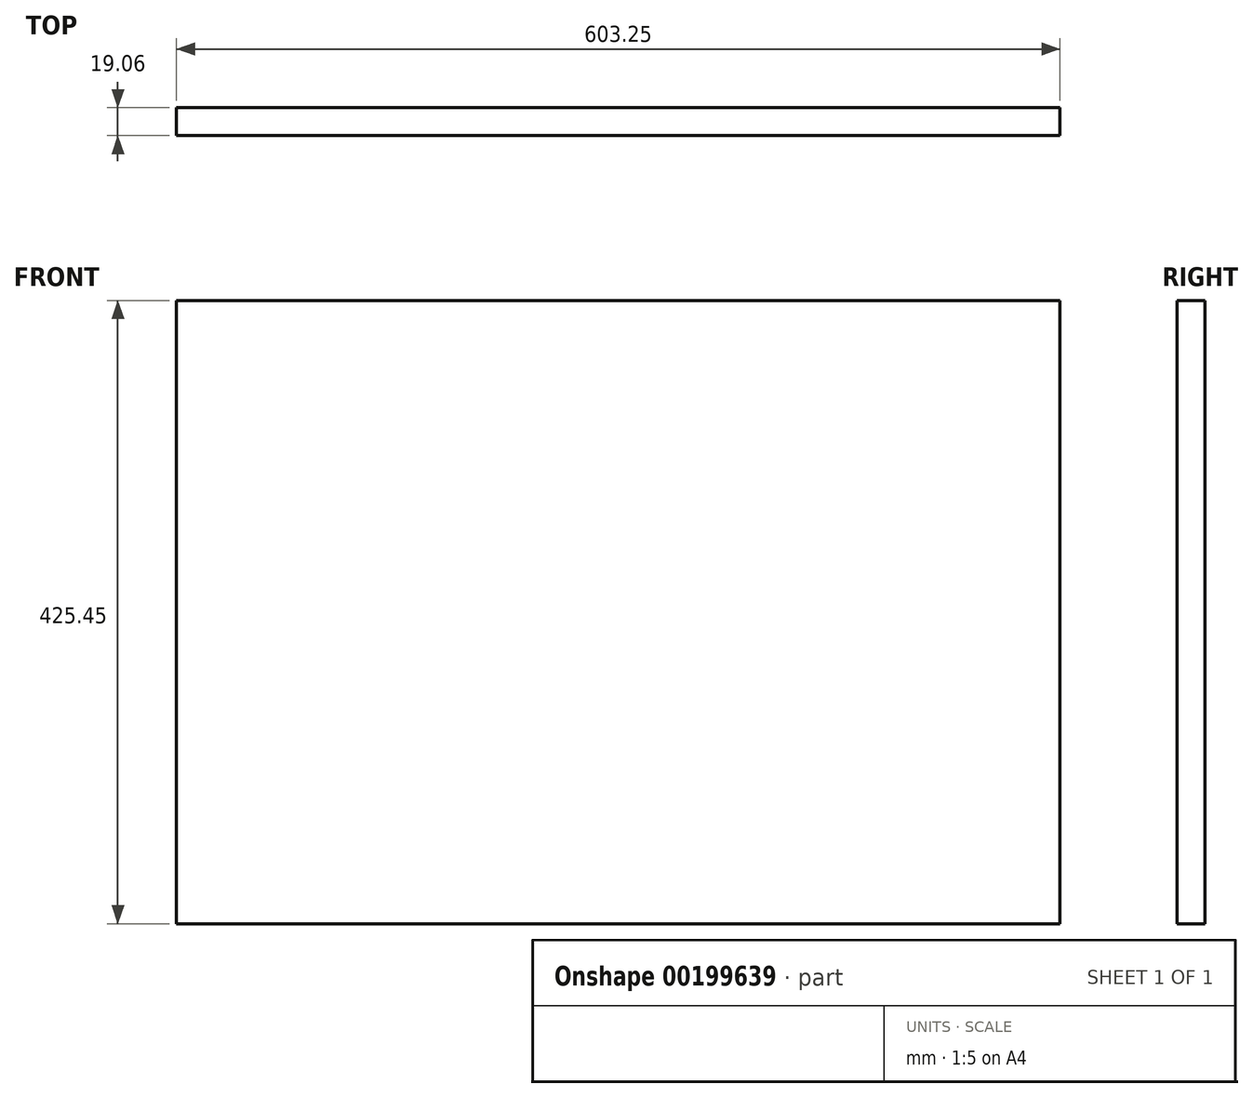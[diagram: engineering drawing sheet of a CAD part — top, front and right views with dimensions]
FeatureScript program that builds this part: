
annotation { "Feature Type Name" : "Feature", "Feature Type Description" : "" }
export const myFeature = defineFeature(function(context is Context, id is Id, definition is map)
    precondition{}
    {
        {
            var Q0;
            Q0=qCreatedBy(makeId("Front.planeOp"),FACE);
            var sketch = newSketch(context, id + "F0", { "sketchPlane" : qUnion([Q0])});
            skLineSegment(sketch, "E0.bottom", {"start": v(-315.58, 182.41) * mm, "end": v(287.67, 182.41) * mm});
            skLineSegment(sketch, "E0.top", {"start": v(-315.58, -243.04) * mm, "end": v(287.67, -243.04) * mm});
            skLineSegment(sketch, "E0.left", {"start": v(-315.58, 182.41) * mm, "end": v(-315.58, -243.04) * mm});
            skLineSegment(sketch, "E0.right", {"start": v(287.67, 182.41) * mm, "end": v(287.67, -243.04) * mm});
            skSolve(sketch);
        }
        {
            var Q0;
            Q0=makeQuery(id+"F0.imprint","IMPRINT",FACE,{"disambiguationData":[TD([[makeQuery(id+"F0.imprint","IMPRINT",EDGE,{"derivedFrom":sQuery(id+"F0.wireOp",EDGE,"E0.bottom")}),-1.0]])]});
            extrude(context, id + "F1", {"entities" : qUnion([Q0]), "endBound" : BoundingType.SYMMETRIC, "depth" : 19.05 * mm});
        }
    });
